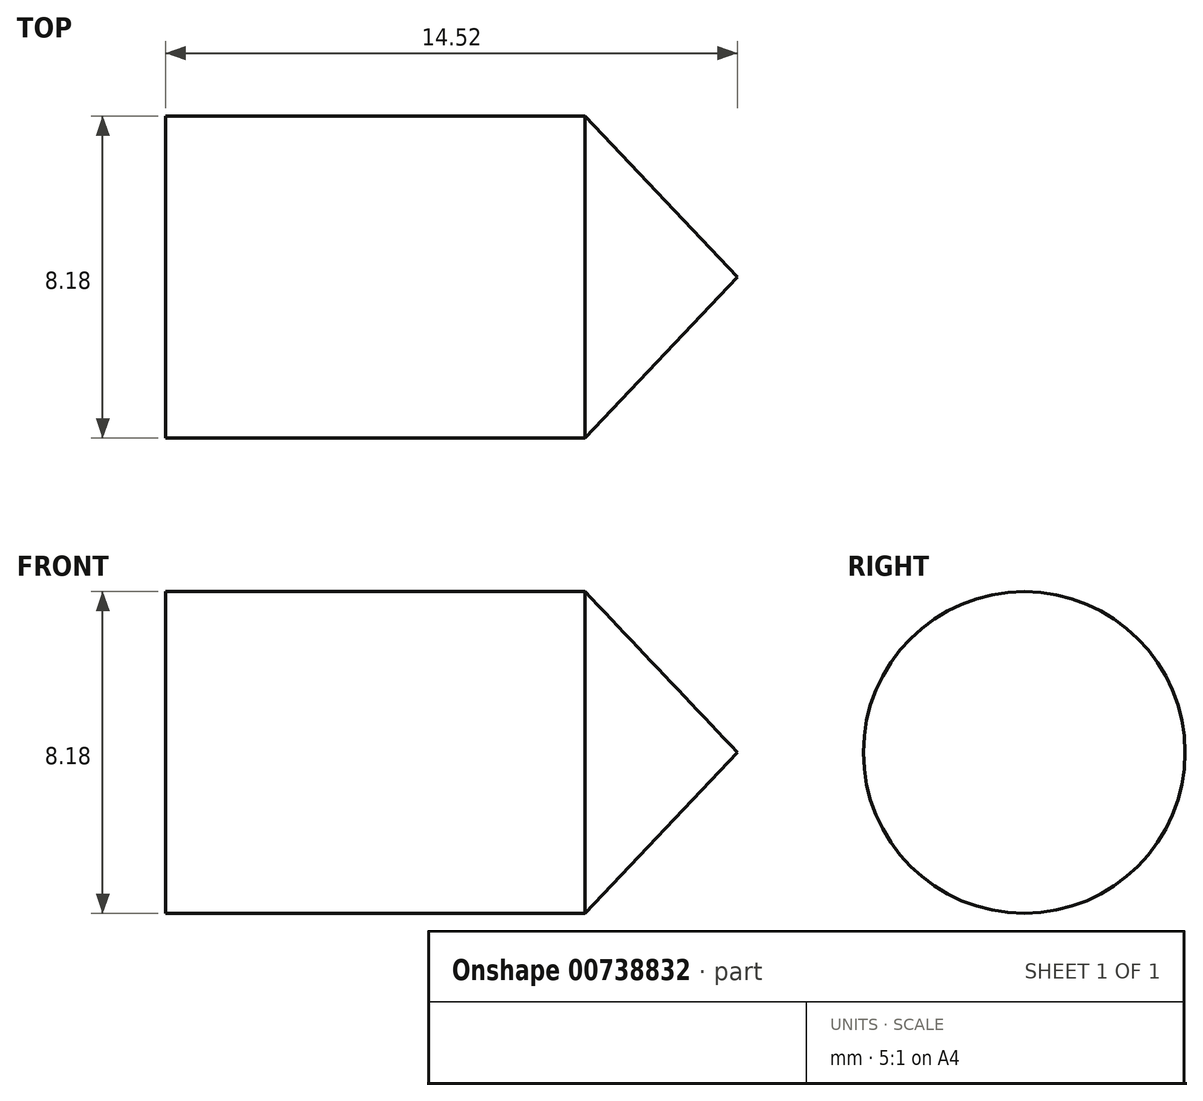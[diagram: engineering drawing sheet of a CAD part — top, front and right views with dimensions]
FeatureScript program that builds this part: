
annotation { "Feature Type Name" : "Feature", "Feature Type Description" : "" }
export const myFeature = defineFeature(function(context is Context, id is Id, definition is map)
    precondition{}
    {
        {
            var Q0;
            Q0=qCreatedBy(makeId("Front.planeOp"),FACE);
            var sketch = newSketch(context, id + "F0", { "sketchPlane" : qUnion([Q0])});
            skLineSegment(sketch, "E0", {"start": v(93.54, 0) * mm, "end": v(-39.2, 0) * mm, "construction": true});
            skLineSegment(sketch, "E1", {"start": v(93.54, 3.22) * mm, "end": v(87.8, 3.25) * mm});
            skLineSegment(sketch, "E2", {"start": v(87.8, 3.25) * mm, "end": v(87.8, 2.25) * mm});
            skLineSegment(sketch, "E3", {"start": v(87.8, 2.25) * mm, "end": v(85.8, 2.25) * mm});
            skLineSegment(sketch, "E4", {"start": v(84.41, 3.25) * mm, "end": v(75.8, 3.25) * mm});
            skLineSegment(sketch, "E5", {"start": v(75.8, 3.25) * mm, "end": v(75.8, 6) * mm});
            skLineSegment(sketch, "E6", {"start": v(75.8, 6) * mm, "end": v(-11.98, 6) * mm});
            skLineSegment(sketch, "E7", {"start": v(-11.98, 3.5) * mm, "end": v(0.02, 3.5) * mm});
            skLineSegment(sketch, "E8", {"start": v(3.29, 0) * mm, "end": v(3.29, 0) * mm});
            skPoint(sketch, "E9", {"position": v(-3.98, 0) * mm});
            skPoint(sketch, "E10", {"position": v(-5.98, 1.96) * mm});
            skPoint(sketch, "E11", {"position": v(-1.98, 1.96) * mm});
            skPoint(sketch, "E12", {"position": v(-1.98, -2.04) * mm});
            skPoint(sketch, "E13", {"position": v(-5.98, -2.04) * mm});
            skLineSegment(sketch, "E14", {"start": v(4.89, 1) * mm, "end": v(34.57, 1) * mm});
            skLineSegment(sketch, "E15", {"start": v(34.57, 1) * mm, "end": v(35.92, 1.5) * mm});
            skLineSegment(sketch, "E16", {"start": v(0.02, 3.5) * mm, "end": v(4.89, 1) * mm});
            skLineSegment(sketch, "E17", {"start": v(84.41, 3.25) * mm, "end": v(85.8, 2.25) * mm});
            skLineSegment(sketch, "E18", {"start": v(-11.98, 6) * mm, "end": v(-11.98, 3.5) * mm});
            skLineSegment(sketch, "E19", {"start": v(93.54, 3.22) * mm, "end": v(95.3, 2.46) * mm});
            skLineSegment(sketch, "E20", {"start": v(95.3, 0) * mm, "end": v(95.3, 2.46) * mm});
            skSolve(sketch);
        }
        {
            var Q0;
            Q0=sQuery(id+"F0.wireOp",EDGE,"vP0A0sck-KfXd-c2yQ-rDDP-f8nhW2mnISOb");
            var Q1;
            Q1=sQuery(id+"F0.wireOp",EDGE,"CmTlwiqP-stsH-PBaX-lvLu-iD5qGkIcsG0C");
            var Q2;
            Q2=sQuery(id+"F0.wireOp",EDGE,"HImPQKQh-nS0p-6pTA-3tRD-cJye2LS2SYvz");
            var Q3;
            Q3=sQuery(id+"F0.wireOp",EDGE,"E4");
            var Q4;
            Q4=sQuery(id+"F0.wireOp",EDGE,"E1");
            var Q5;
            Q5=sQuery(id+"F0.wireOp",EDGE,"E7");
            var Q6;
            Q6=sQuery(id+"F0.wireOp",EDGE,"YZweMkIF-1W4O-kEtk-cVjo-jittVB30vj1x");
            var Q7;
            Q7=sQuery(id+"F0.wireOp",EDGE,"c2HSSA3k-kEJK-0HBW-NdYC-9stfZNvT4Cat");
            var Q8;
            Q8=sQuery(id+"F0.wireOp",EDGE,"BSc4jtBH-HqFf-l5WU-sChG-K1G4yU2T35oV");
            var Q9;
            Q9=sQuery(id+"F0.wireOp",EDGE,"E2");
            var Q10;
            Q10=sQuery(id+"F0.wireOp",EDGE,"ejMcucVx-R0F9-RKGx-V5xH-kpR7UxxP9j1Y");
            var Q11;
            Q11=sQuery(id+"F0.wireOp",EDGE,"E5");
            var Q12;
            Q12=sQuery(id+"F0.wireOp",EDGE,"E3");
            var Q13;
            Q13=sQuery(id+"F0.wireOp",EDGE,"E6");
            var Q14;
            Q14=sQuery(id+"F0.wireOp",EDGE,"xSa9r4se-SWCZ-dLS2-2pP1-INlK1mxo1qs8");
            var Q15;
            Q15=sQuery(id+"F0.wireOp",EDGE,"E0");
            revolve(context, id + "F1", {"bodyType" : ToolBodyType.SURFACE, "surfaceOperationType" : NewSurfaceOperationType.NEW, "surfaceEntities" : qUnion([Q0, Q1, Q2, Q3, Q4, Q5, Q6, Q7, Q8, Q9, Q10, Q11, Q12, Q13, Q14]), "axis" : qUnion([Q15]), "revolveType" : RevolveType.FULL});
        }
        {
            var Q0;
            Q0=qCreatedBy(makeId("Front.planeOp"),FACE);
            var sketch = newSketch(context, id + "F2", { "sketchPlane" : qUnion([Q0])});
            skLineSegment(sketch, "E21", {"start": v(-16.66, 4.09) * mm, "end": v(-27.31, 4.09) * mm});
            skLineSegment(sketch, "E22", {"start": v(-27.31, 0) * mm, "end": v(-12.79, 0) * mm});
            skLineSegment(sketch, "E23", {"start": v(-12.79, 0) * mm, "end": v(-16.66, 4.09) * mm});
            skLineSegment(sketch, "E24", {"start": v(-27.31, 0) * mm, "end": v(-27.31, 4.09) * mm});
            skLineSegment(sketch, "E25", {"start": v(-27.31, 4.09) * mm, "end": v(-16.66, 4.09) * mm});
            skSolve(sketch);
        }
        {
            var Q0;
            Q0=makeQuery(id+"F2.imprint","IMPRINT",FACE,{"disambiguationData":[TD([[makeQuery(id+"F2.imprint","IMPRINT",EDGE,{"derivedFrom":sQuery(id+"F2.wireOp",EDGE,"E22")}),1.0]])]});
            var Q1;
            Q1=sQuery(id+"F0.wireOp",EDGE,"E0");
            revolve(context, id + "F3", {"surfaceOperationType" : NewSurfaceOperationType.NEW, "entities" : qUnion([Q0]), "axis" : qUnion([Q1]), "revolveType" : RevolveType.FULL});
        }
    });
